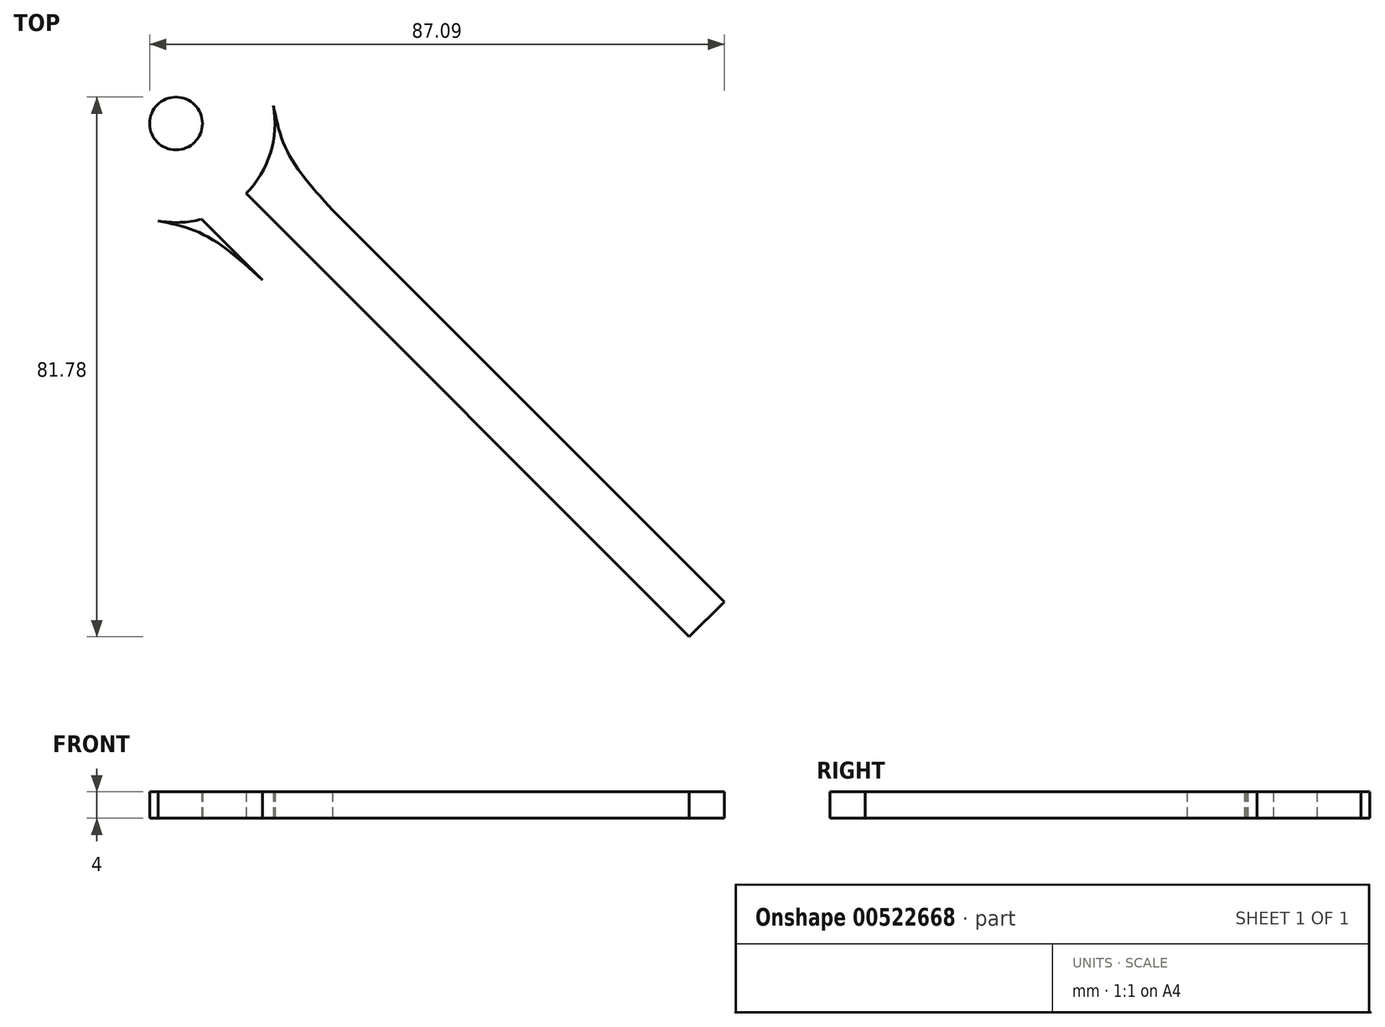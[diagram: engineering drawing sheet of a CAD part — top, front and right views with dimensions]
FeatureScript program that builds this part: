
annotation { "Feature Type Name" : "Feature", "Feature Type Description" : "" }
export const myFeature = defineFeature(function(context is Context, id is Id, definition is map)
    precondition{}
    {
        {
            var Q0;
            Q0=qCreatedBy(makeId("Top.planeOp"),FACE);
            var sketch = newSketch(context, id + "F0", { "sketchPlane" : qUnion([Q0])});
            skPoint(sketch, "E0", {"position": v(-9.35, -7.3) * mm});
            skLineSegment(sketch, "E1", {"start": v(11.4, -28.05) * mm, "end": v(-9.35, -7.3) * mm});
            skLineSegment(sketch, "E2", {"start": v(11.4, -28.05) * mm, "end": v(-66.39, 49.73) * mm});
            skCircle(sketch, "E3.MirrorC", {"center": v(-66.39, 49.73) * mm, "radius": 4 * mm});
            skLineSegment(sketch, "E4.MirrorCS", {"start": v(-66.39, 57.48) * mm, "end": v(-66.39, 59.23) * mm});
            skArc(sketch, "E5.MirrorCS", {"start": v(-51.63, 52.41) * mm, "mid": v(-51.95, 53.78) * mm, "end": v(-52.39, 55.1) * mm});
            skLineSegment(sketch, "E6.MirrorCS", {"start": v(-72.64, 49.73) * mm, "end": v(-74.39, 49.73) * mm});
            skLineSegment(sketch, "E7.MirrorCS", {"start": v(-60.14, 49.73) * mm, "end": v(-58.39, 49.73) * mm});
            skCircle(sketch, "E8.MirrorC", {"center": v(-66.39, 59.23) * mm, "radius": 1.75 * mm});
            skArc(sketch, "E9.MirrorCS", {"start": v(-80.4, 55.1) * mm, "mid": v(-81.38, 50.3) * mm, "end": v(-80.76, 45.44) * mm});
            skCircle(sketch, "E10.MirrorC", {"center": v(-58.39, 49.73) * mm, "radius": 1.75 * mm});
            skFitSpline(sketch, "E11.MirrorCS", {"points": [v(-72.48, 36.02) * mm, v(-73.76, 39.98) * mm, v(-80.76, 45.44) * mm], "startDerivative": vector(-1.43, 9.82) * mm, "endDerivative": vector(-14.32, 9.05) * mm});
            skArc(sketch, "E12.MirrorCS", {"start": v(-60.9, 63.69) * mm, "mid": v(-66.27, 64.73) * mm, "end": v(-71.65, 63.78) * mm});
            skFitSpline(sketch, "E13.MirrorCS", {"points": [v(-80.4, 55.1) * mm, v(-75.95, 58.6) * mm, v(-71.65, 63.78) * mm], "startDerivative": vector(9.53, 6.72) * mm, "endDerivative": vector(7.98, 10.57) * mm});
            skCircle(sketch, "E14.MirrorC", {"center": v(-74.39, 49.73) * mm, "radius": 1.75 * mm});
            skFitSpline(sketch, "E15.MirrorCS", {"points": [v(-42.68, 36.63) * mm, v(-49.41, 45.26) * mm, v(-51.63, 52.41) * mm], "startDerivative": vector(-14.32, 15.77) * mm, "endDerivative": vector(-3.24, 15.8) * mm});
            skLineSegment(sketch, "E16.MirrorCS", {"start": v(-66.39, 41.98) * mm, "end": v(-66.39, 40.23) * mm});
            skLineSegment(sketch, "E17.MirrorCS", {"start": v(-62.5, 35.24) * mm, "end": v(-65.84, 38.57) * mm});
            skFitSpline(sketch, "E18.MirrorCS", {"points": [v(-52.39, 55.1) * mm, v(-55.96, 55.96) * mm, v(-60.9, 63.69) * mm], "startDerivative": vector(-9.44, 0.18) * mm, "endDerivative": vector(-7.72, 15.8) * mm});
            skCircle(sketch, "E19.MirrorC", {"center": v(-66.39, 40.23) * mm, "radius": 1.75 * mm});
            skArc(sketch, "E20.MirrorCS", {"start": v(-51.63, 52.41) * mm, "mid": v(-55.78, 39.12) * mm, "end": v(-69.07, 34.97) * mm});
            skFitSpline(sketch, "E21.MirrorCS", {"points": [v(-53.29, 26.02) * mm, v(-61.92, 32.75) * mm, v(-69.07, 34.97) * mm], "startDerivative": vector(-15.77, 14.32) * mm, "endDerivative": vector(-15.8, 3.24) * mm});
            skLineSegment(sketch, "E22.MirrorCS", {"start": v(6.09, -33.36) * mm, "end": v(-71.7, 44.43) * mm});
            skArc(sketch, "E23.MirrorCS", {"start": v(-72.48, 36.02) * mm, "mid": v(-59.92, 36.2) * mm, "end": v(-51.9, 45.85) * mm});
            skLineSegment(sketch, "E24.MirrorCS", {"start": v(6.09, -33.36) * mm, "end": v(-53.29, 26.02) * mm});
            skPoint(sketch, "E25.MirrorP", {"position": v(-71.7, 44.43) * mm});
            skLineSegment(sketch, "E26.MirrorCS", {"start": v(16.7, -22.75) * mm, "end": v(-42.68, 36.63) * mm});
            skPoint(sketch, "E27.MirrorP", {"position": v(-61.09, 55.03) * mm});
            skLineSegment(sketch, "E28.MirrorCS", {"start": v(11.4, -28.05) * mm, "end": v(-55.78, 39.12) * mm});
            skLineSegment(sketch, "E29", {"start": v(6.09, -33.36) * mm, "end": v(16.7, -22.75) * mm});
            skSolve(sketch);
        }
        {
            var Q0;
            Q0=makeQuery(id+"F0.imprint","IMPRINT",FACE,{"disambiguationData":[TD([[makeQuery(id+"F0.imprint","IMPRINT",EDGE,{"derivedFrom":sQuery(id+"F0.wireOp",EDGE,"E3.MirrorC")}),1.0]])]});
            var Q1;
            {var subQ4=sQuery(id+"F0.wireOp",EDGE,"E24.MirrorCS");Q1=makeQuery(id+"F0.imprint","IMPRINT",FACE,{"disambiguationData":[TD([[makeQuery(id+"F0.imprint","IMPRINT",EDGE,{"derivedFrom":subQ4}),-1.0]])]});}
            var Q2;
            Q2=makeQuery(id+"F0.imprint","IMPRINT",FACE,{"disambiguationData":[TD([[makeQuery(id+"F0.imprint","IMPRINT",EDGE,{"derivedFrom":sQuery(id+"F0.wireOp",EDGE,"E15.MirrorCS")}),1.0]])]});
            var Q3;
            {var subQ0=sQuery(id+"F0.wireOp",EDGE,"E21.MirrorCS");Q3=makeQuery(id+"F0.imprint","IMPRINT",FACE,{"disambiguationData":[TD([[makeQuery(id+"F0.imprint","IMPRINT",EDGE,{"derivedFrom":subQ0}),-1.0]])]});}
            extrude(context, id + "F1", {"entities" : qUnion([Q0, Q1, Q2, Q3]), "depth" : 4 * mm, "offsetDistance" : 25 * mm});
        }
    });
